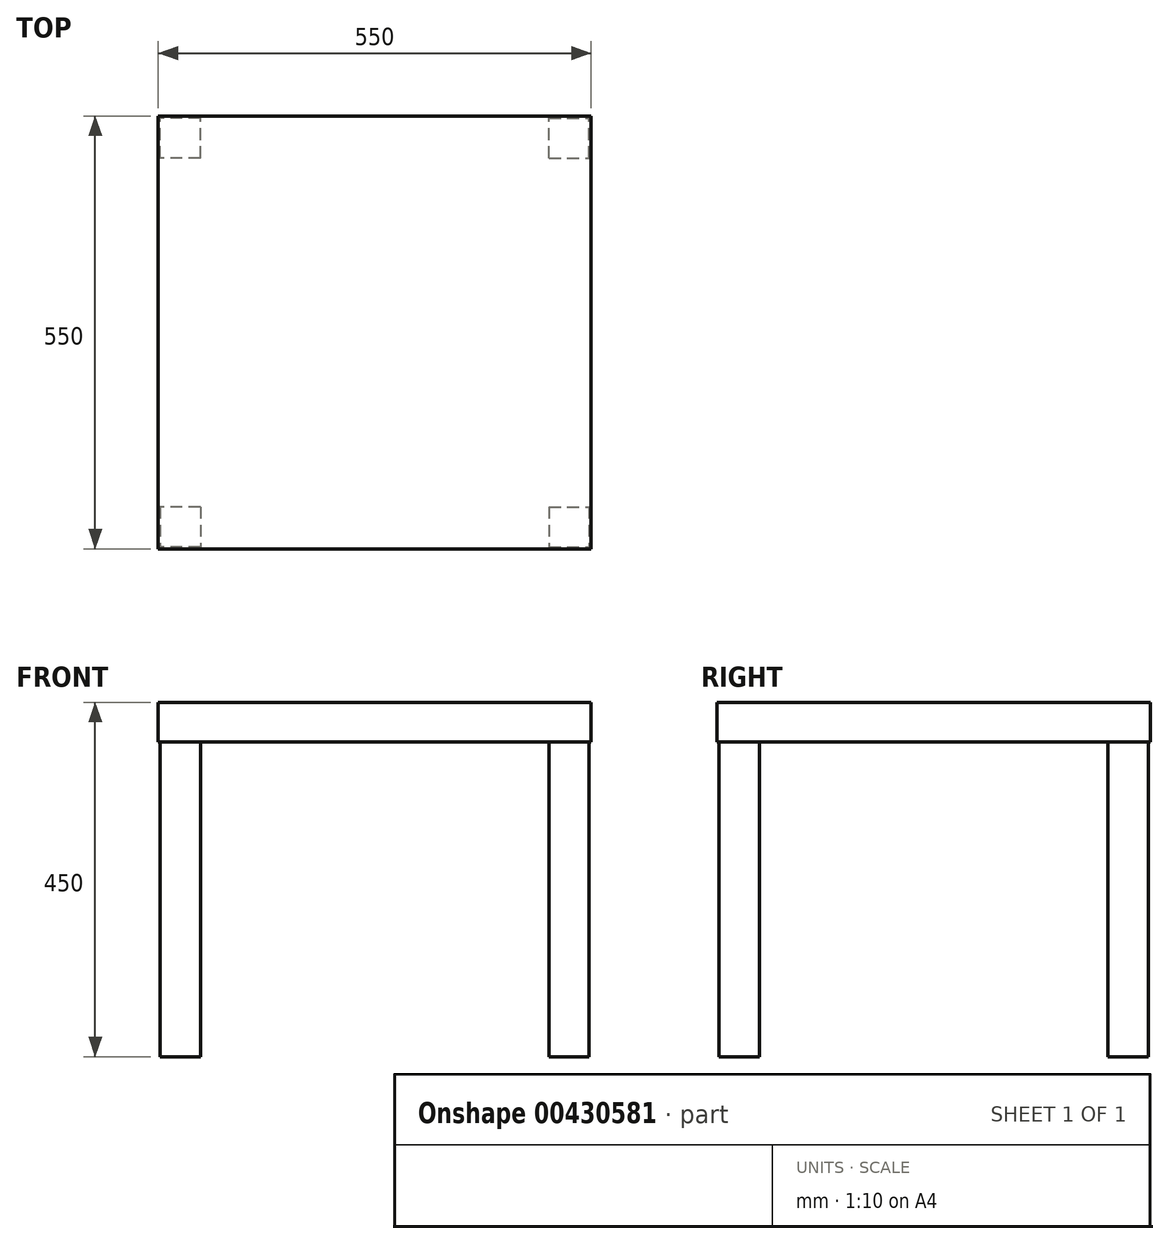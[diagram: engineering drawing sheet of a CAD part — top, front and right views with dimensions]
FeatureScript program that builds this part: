
annotation { "Feature Type Name" : "Feature", "Feature Type Description" : "" }
export const myFeature = defineFeature(function(context is Context, id is Id, definition is map)
    precondition{}
    {
        {
            var Q0;
            Q0=qCreatedBy(makeId("Top.planeOp"),FACE);
            var sketch = newSketch(context, id + "F0", { "sketchPlane" : qUnion([Q0])});
            skLineSegment(sketch, "E0.bottom", {"start": v(275, -275) * mm, "end": v(-275, -275) * mm});
            skLineSegment(sketch, "E0.top", {"start": v(275, 275) * mm, "end": v(-275, 275) * mm});
            skLineSegment(sketch, "E0.left", {"start": v(275, -275) * mm, "end": v(275, 275) * mm});
            skLineSegment(sketch, "E0.right", {"start": v(-275, -275) * mm, "end": v(-275, 275) * mm});
            skPoint(sketch, "E0.middle", {"position": v(0, 0) * mm});
            skSolve(sketch);
        }
        {
            var Q0;
            Q0=makeQuery(id+"F0.imprint","IMPRINT",FACE,{"disambiguationData":[TD([[makeQuery(id+"F0.imprint","IMPRINT",EDGE,{"derivedFrom":sQuery(id+"F0.wireOp",EDGE,"E0.bottom")}),-1.0]])]});
            extrude(context, id + "F1", {"entities" : qUnion([Q0]), "depth" : 50 * mm});
        }
        {
            var Q0;
            Q0=makeQuery(id+"F1.opExtrude","CAP_FACE",FACE,{"disambiguationData":[OSD([sQuery(id+"F0.wireOp",EDGE,"E0.bottom"),sQuery(id+"F0.wireOp",EDGE,"E0.top"),sQuery(id+"F0.wireOp",EDGE,"E0.left"),sQuery(id+"F0.wireOp",EDGE,"E0.right")])],"isStart":true});
            var sketch = newSketch(context, id + "F2", { "sketchPlane" : qUnion([Q0])});
            skLineSegment(sketch, "E1.bottom", {"start": v(-221.5, 221.5) * mm, "end": v(-272.5, 221.5) * mm});
            skLineSegment(sketch, "E1.top", {"start": v(-221.5, 272.5) * mm, "end": v(-272.5, 272.5) * mm});
            skLineSegment(sketch, "E1.left", {"start": v(-221.5, 221.5) * mm, "end": v(-221.5, 272.5) * mm});
            skLineSegment(sketch, "E1.right", {"start": v(-272.5, 221.5) * mm, "end": v(-272.5, 272.5) * mm});
            skPoint(sketch, "E1.middle", {"position": v(-247, 247) * mm});
            skLineSegment(sketch, "E2.MirrorCS", {"start": v(221.5, 272.5) * mm, "end": v(272.5, 272.5) * mm});
            skLineSegment(sketch, "E3.MirrorCS", {"start": v(272.5, 221.5) * mm, "end": v(272.5, 272.5) * mm});
            skLineSegment(sketch, "E4.MirrorCS", {"start": v(221.5, 221.5) * mm, "end": v(221.5, 272.5) * mm});
            skLineSegment(sketch, "E5.MirrorCS", {"start": v(221.5, 221.5) * mm, "end": v(272.5, 221.5) * mm});
            skPoint(sketch, "E6.MirrorP", {"position": v(247, 247) * mm});
            skLineSegment(sketch, "E7.MirrorCS", {"start": v(221.5, -272.5) * mm, "end": v(272.5, -272.5) * mm});
            skLineSegment(sketch, "E8.MirrorCS", {"start": v(272.5, -221.5) * mm, "end": v(272.5, -272.5) * mm});
            skLineSegment(sketch, "E9.MirrorCS", {"start": v(221.5, -221.5) * mm, "end": v(221.5, -272.5) * mm});
            skLineSegment(sketch, "E10.MirrorCS", {"start": v(221.5, -221.5) * mm, "end": v(272.5, -221.5) * mm});
            skPoint(sketch, "E11.MirrorP", {"position": v(247, -247) * mm});
            skLineSegment(sketch, "E12.MirrorCS", {"start": v(-221.5, -221.5) * mm, "end": v(-272.5, -221.5) * mm});
            skPoint(sketch, "E13.MirrorP", {"position": v(-247, -247) * mm});
            skLineSegment(sketch, "E14.MirrorCS", {"start": v(-221.5, -272.5) * mm, "end": v(-272.5, -272.5) * mm});
            skLineSegment(sketch, "E15.MirrorCS", {"start": v(-272.5, -221.5) * mm, "end": v(-272.5, -272.5) * mm});
            skLineSegment(sketch, "E16.MirrorCS", {"start": v(-221.5, -221.5) * mm, "end": v(-221.5, -272.5) * mm});
            skSolve(sketch);
        }
        {
            var Q0;
            Q0 = qSketchRegion(id + "F2", true);
            extrude(context, id + "F3", {"entities" : qUnion([Q0]), "operationType" : NewBodyOperationType.ADD, "depth" : 400 * mm});
        }
    });
